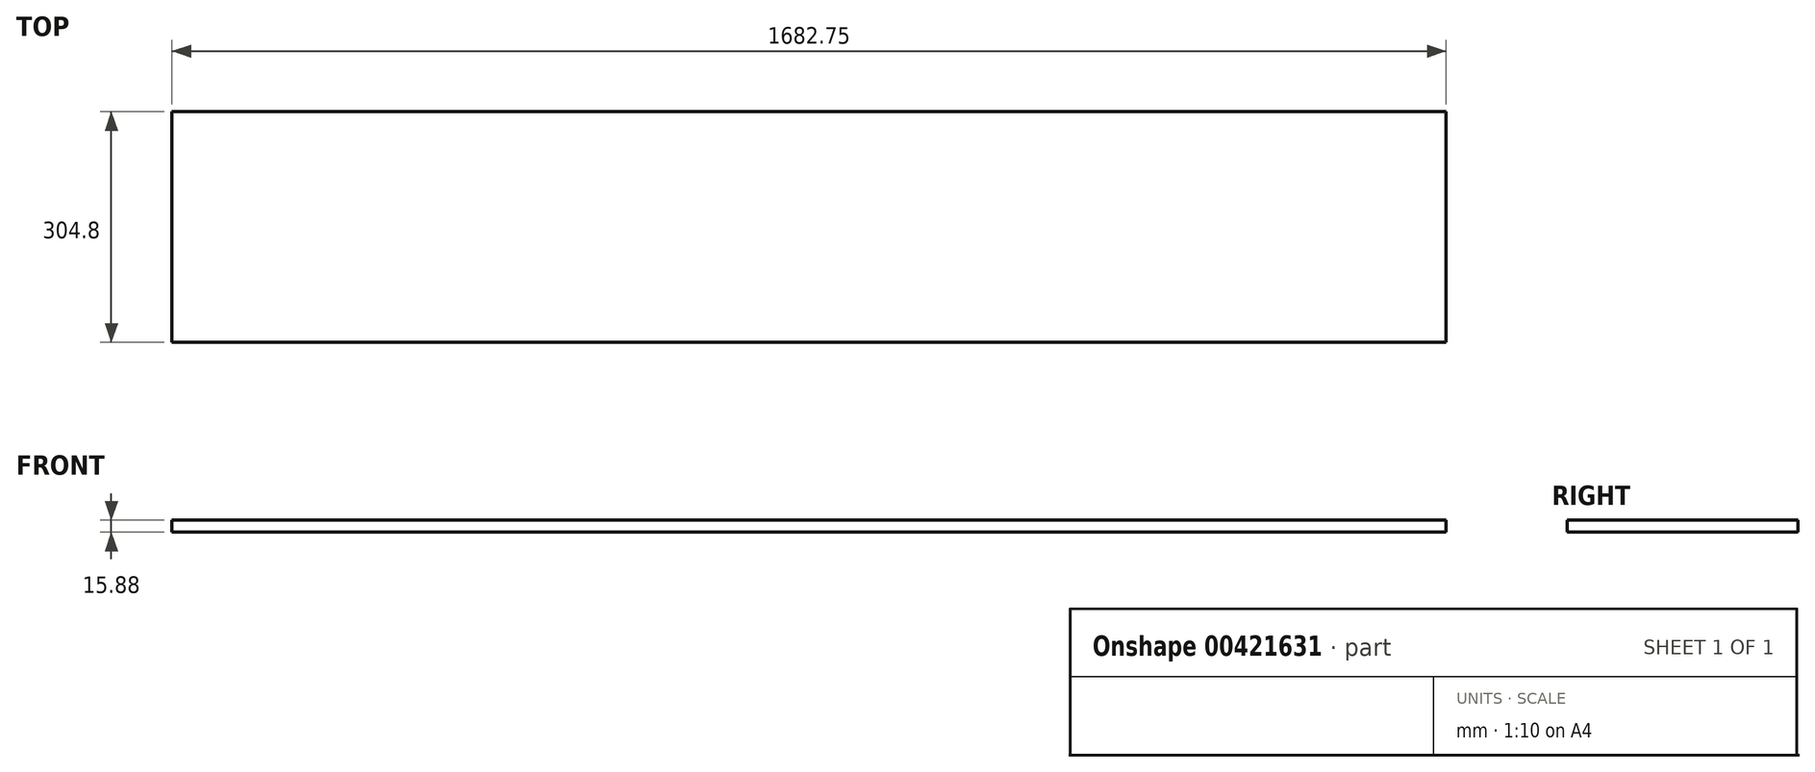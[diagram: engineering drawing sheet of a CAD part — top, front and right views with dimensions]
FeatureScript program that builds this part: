
annotation { "Feature Type Name" : "Feature", "Feature Type Description" : "" }
export const myFeature = defineFeature(function(context is Context, id is Id, definition is map)
    precondition{}
    {
        {
            var Q0;
            Q0=qCreatedBy(makeId("Front.planeOp"),FACE);
            var sketch = newSketch(context, id + "F0", { "sketchPlane" : qUnion([Q0])});
            skLineSegment(sketch, "E0.bottom", {"start": v(0, 0) * mm, "end": v(1682.75, 0) * mm});
            skLineSegment(sketch, "E0.top", {"start": v(0, 15.88) * mm, "end": v(1682.75, 15.88) * mm});
            skLineSegment(sketch, "E0.left", {"start": v(0, 0) * mm, "end": v(0, 15.88) * mm});
            skLineSegment(sketch, "E0.right", {"start": v(1682.75, 0) * mm, "end": v(1682.75, 15.88) * mm});
            skSolve(sketch);
        }
        {
            var Q0;
            Q0 = qSketchRegion(id + "F0", true);
            extrude(context, id + "F1", {"entities" : qUnion([Q0]), "depth" : 304.8 * mm});
        }
    });
